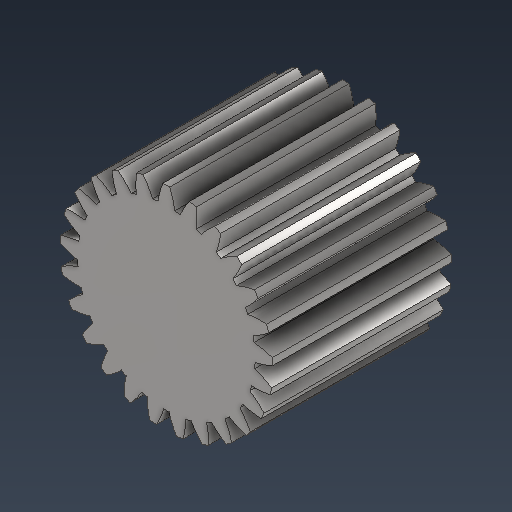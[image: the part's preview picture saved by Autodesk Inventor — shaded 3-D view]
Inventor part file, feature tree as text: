
AUTODESK INVENTOR PART (.ipt)
format: ipt  version: 2021 (Build 250183000, 183)  size: 324,096 bytes
history: native  units: mm (DEFAULTED — no unit token found)
features: plane x3, other x3, sketch x2, extrude x1
ambient origin geometry x8: Origin, YZ Plane, XZ Plane, XY Plane, X Axis, Y Axis, Z Axis, Center Point
bodies: Solid1 (feature_tree)
feature tree (9):
  extrude  "Extrusion1"  Depth=2.5mm TaperAngle=0.0deg
  plane  "Work Plane2"
  plane  "Work Plane8"
  plane  "Work Plane9"
  other  "Engrenagem reta"
  sketch  "Sketch1"  dims[d0=2.968907mm d1=2.5mm d2=0.0mm]
  sketch  "Sketch2"  dims[d3=2.75mm d4=10.0mm d5=0.0mm d16=3.598mm d17=0.0mm d34=1.256637mm d39=0.0mm d41=0.0mm d43=3.598mm d46=3.598mm d47=0.0mm d48=0.0mm]
  other  "Srf1"
  other  "Diâmetro do flanco"
